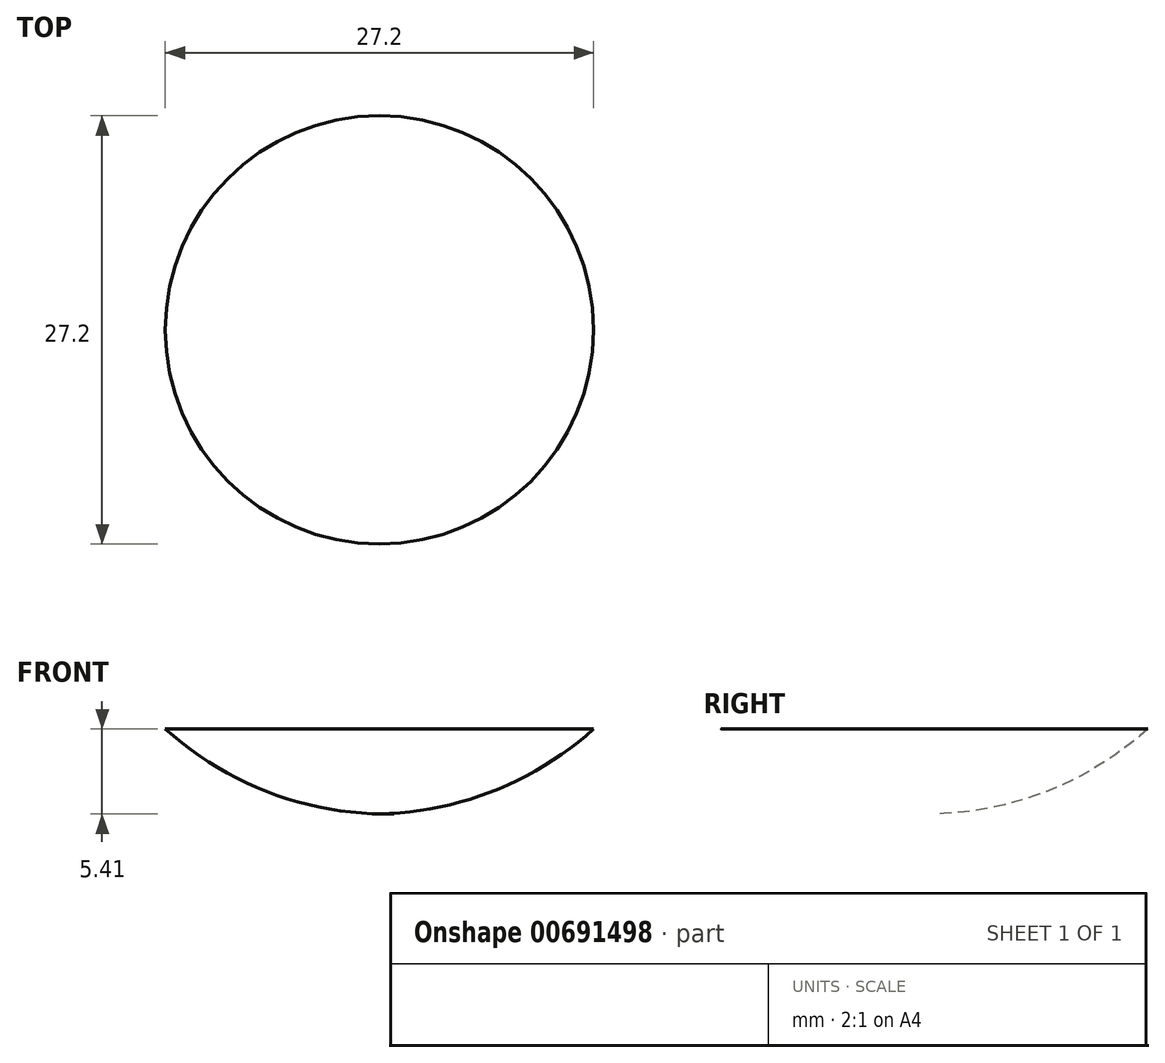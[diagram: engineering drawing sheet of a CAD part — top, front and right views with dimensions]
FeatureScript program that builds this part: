
annotation { "Feature Type Name" : "Feature", "Feature Type Description" : "" }
export const myFeature = defineFeature(function(context is Context, id is Id, definition is map)
    precondition{}
    {
        {
            var Q0;
            Q0=qCreatedBy(makeId("Front.planeOp"),FACE);
            var sketch = newSketch(context, id + "F0", { "sketchPlane" : qUnion([Q0])});
            skLineSegment(sketch, "E0", {"start": v(-13.6, 25.4) * mm, "end": v(0, 25.4) * mm});
            skPoint(sketch, "E1", {"position": v(0, 20) * mm});
            skArc(sketch, "E2", {"start": v(-13.6, 25.4) * mm, "mid": v(-7.29, 21.48) * mm, "end": v(0, 20) * mm});
            skLineSegment(sketch, "E3", {"start": v(0, 25.4) * mm, "end": v(0, 20) * mm});
            skSolve(sketch);
        }
        {
            var Q0;
            Q0=qCreatedBy(makeId("Front.planeOp"),FACE);
            var sketch = newSketch(context, id + "F1", { "sketchPlane" : qUnion([Q0])});
            skLineSegment(sketch, "E4", {"start": v(0, 0) * mm, "end": v(0, -9.62) * mm});
            skSolve(sketch);
        }
        {
            var Q0;
            Q0 = qSketchRegion(id + "F1", true);
            var Q1;
            Q1 = qSketchRegion(id + "F0", true);
            var Q2;
            Q2=sQuery(id+"F1.wireOp",EDGE,"E4");
            revolve(context, id + "F2", {"entities" : qUnion([Q0, Q1]), "axis" : qUnion([Q2]), "revolveType" : RevolveType.FULL});
        }
    });
